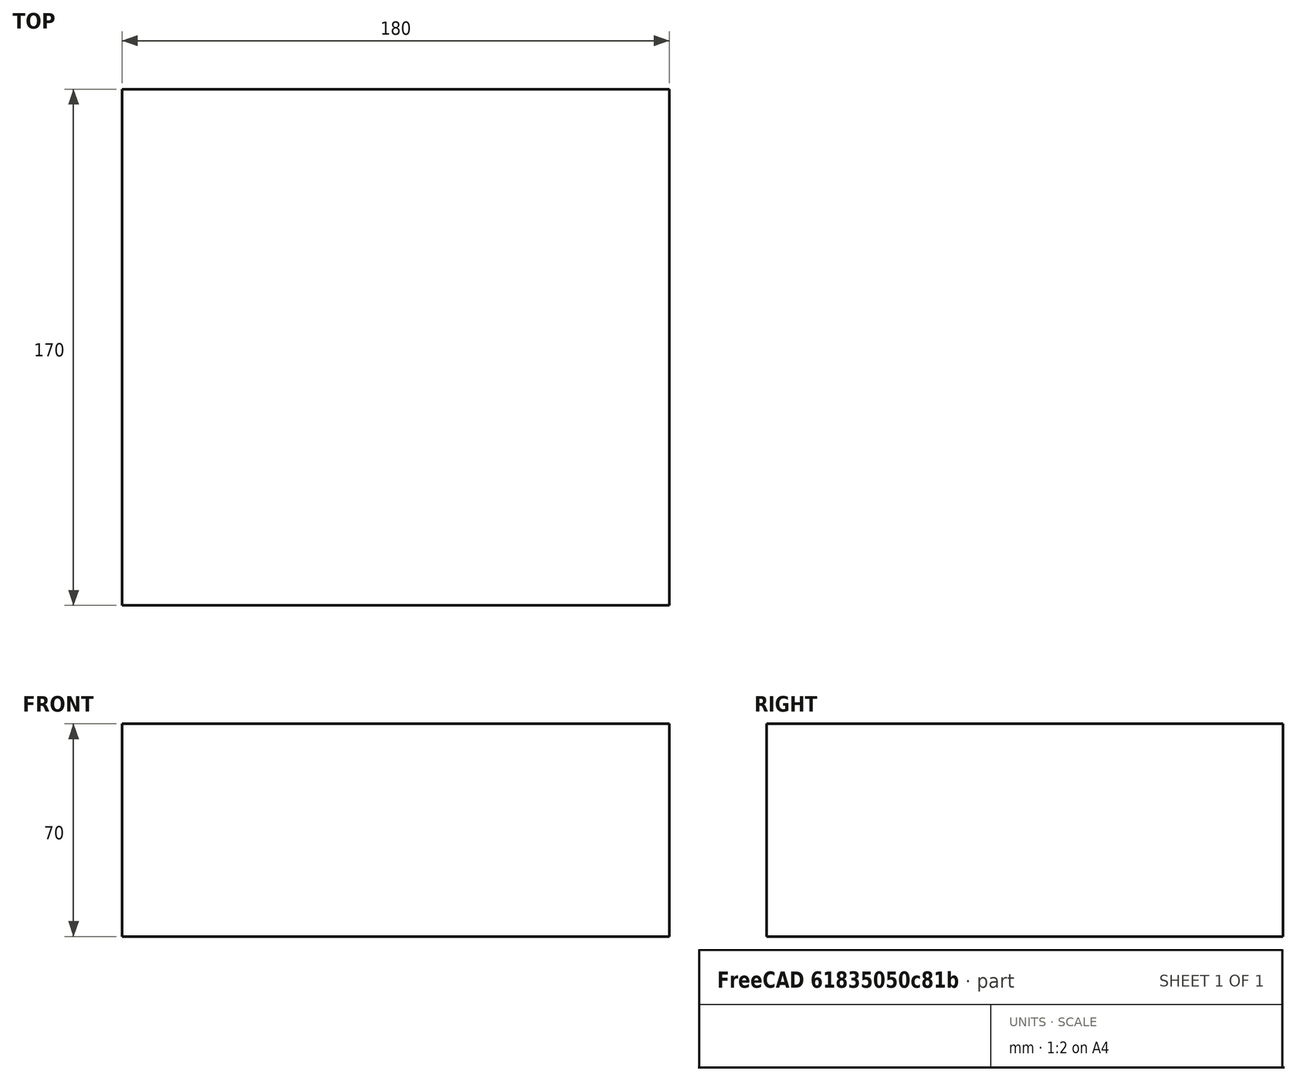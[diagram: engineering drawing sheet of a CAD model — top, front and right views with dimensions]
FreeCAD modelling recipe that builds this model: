
FCSTD DOCUMENT  (FreeCAD 0.18R4 (GitTag))
Label: Box-C
License: All rights reserved
LicenseURL: http://en.wikipedia.org/wiki/All_rights_reserved
objects: Sketcher::SketchObject×1, PartDesign::Pad×1, PartDesign::Body×1
note: 4 computed .brp shape members not serialized (recipe doc carries the construction recipe); baked Part::Feature solids carry a one-line shape summary decoded from their .brp

FEATURE [Sketcher::SketchObject] Sketch
  MapMode = 5
  Support = -> [XY_Plane]
  sketch-geometry (4):
    g0: LineSegment StartX=0 StartY=0 StartZ=0 EndX=-180 EndY=0 EndZ=0
    g1: LineSegment StartX=-180 StartY=0 StartZ=0 EndX=-180 EndY=170 EndZ=0
    g2: LineSegment StartX=-180 StartY=170 StartZ=0 EndX=0 EndY=170 EndZ=0
    g3: LineSegment StartX=0 StartY=170 StartZ=0 EndX=0 EndY=0 EndZ=0
  constraints (10):
    c: Coincident(g0,g1)
    c: Coincident(g1,g2)
    c: Coincident(g2,g3)
    c: Coincident(g3,g0)
    c: Horizontal(g2)
    c: Vertical(g1)
    c: Distance(g0) = 180
    c: Distance(g1) = 170
    c: Tangent(g3,g-2)
    c: Tangent(g0,g-1)
FEATURE [PartDesign::Pad] Pad
  Length = 70
  Length2 = 100
  Profile = -> Sketch
  Type = 0
FEATURE [PartDesign::Body] Body
  Group = -> [Sketch,Pad]
  Origin = -> Origin
  Tip = -> Pad
